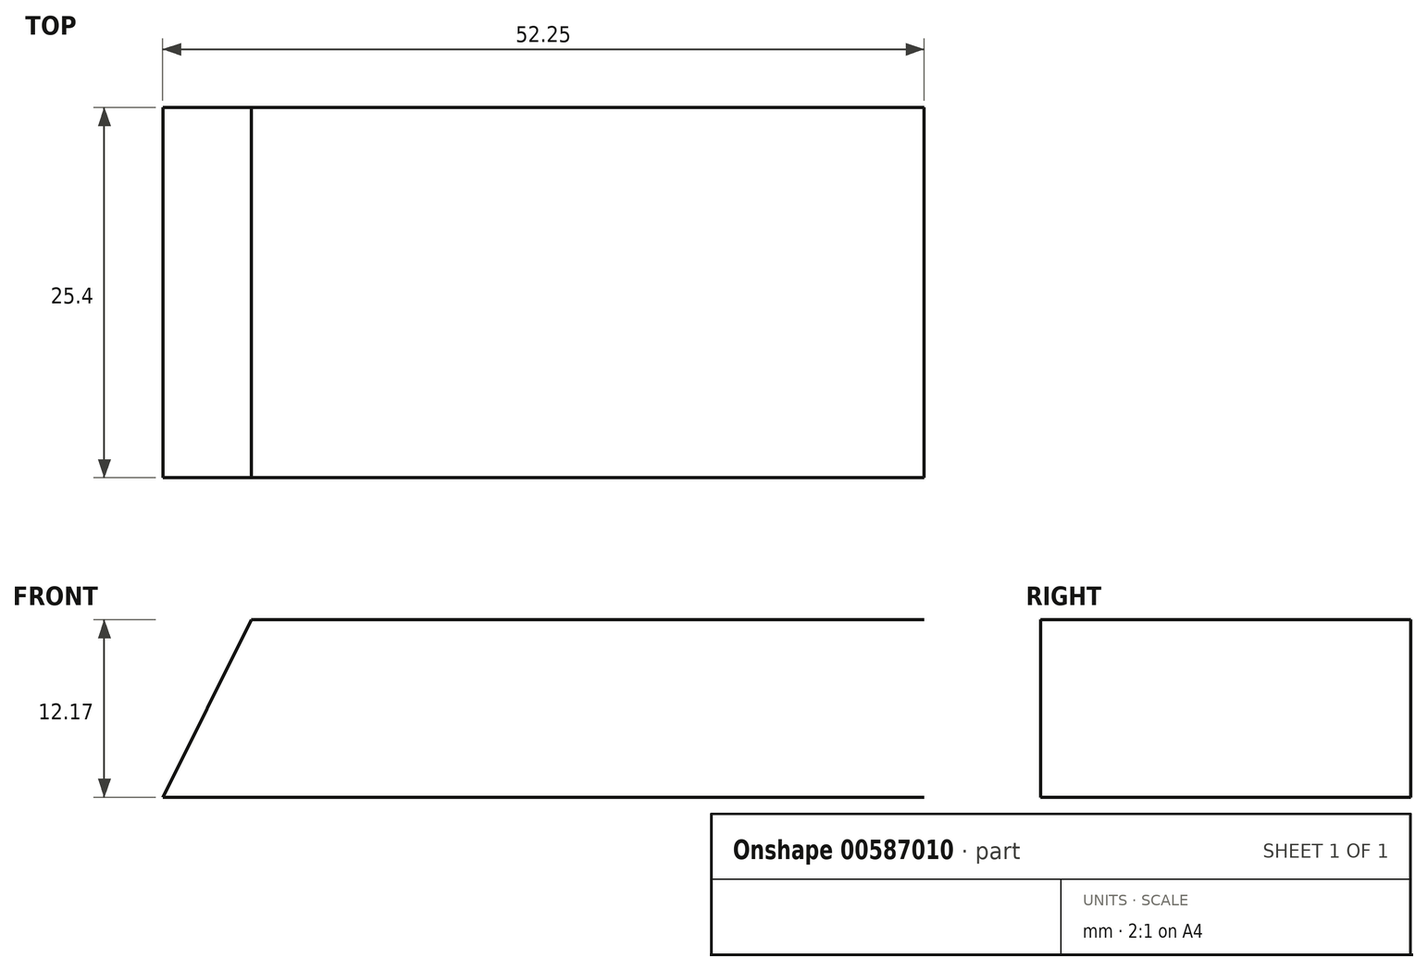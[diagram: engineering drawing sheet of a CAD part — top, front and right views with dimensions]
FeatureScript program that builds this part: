
annotation { "Feature Type Name" : "Feature", "Feature Type Description" : "" }
export const myFeature = defineFeature(function(context is Context, id is Id, definition is map)
    precondition{}
    {
        {
            var Q0;
            Q0=qCreatedBy(makeId("Front.planeOp"),FACE);
            var sketch = newSketch(context, id + "F0", { "sketchPlane" : qUnion([Q0])});
            skLineSegment(sketch, "E0", {"start": v(0, 0) * mm, "end": v(-46.16, 0) * mm});
            skLineSegment(sketch, "E1", {"start": v(-46.16, 0) * mm, "end": v(-52.25, -12.17) * mm});
            skLineSegment(sketch, "E2", {"start": v(-52.25, -12.17) * mm, "end": v(0, -12.17) * mm});
            skSolve(sketch);
        }
        {
            var Q0;
            Q0=sQuery(id+"F0.wireOp",EDGE,"E2");
            var Q1;
            Q1=sQuery(id+"F0.wireOp",EDGE,"E1");
            var Q2;
            Q2=sQuery(id+"F0.wireOp",EDGE,"E0");
            extrude(context, id + "F1", {"bodyType" : ToolBodyType.SURFACE, "surfaceEntities" : qUnion([Q0, Q1, Q2]), "depth" : 25.4 * mm, "offsetDistance" : 25.4 * mm});
        }
    });
